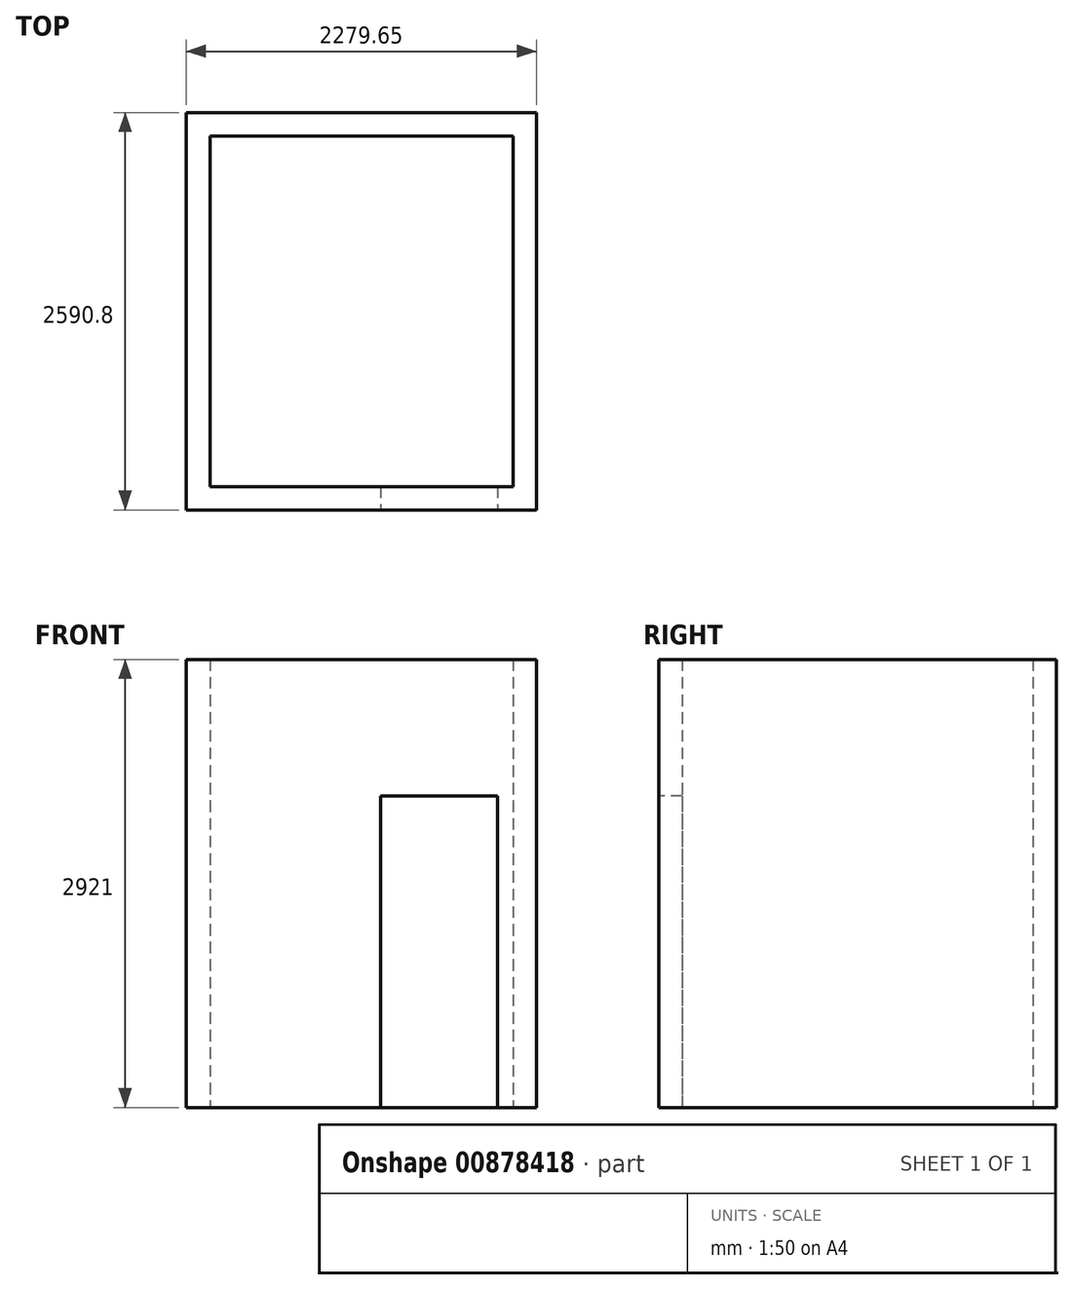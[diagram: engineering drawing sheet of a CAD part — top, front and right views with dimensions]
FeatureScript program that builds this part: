
annotation { "Feature Type Name" : "Feature", "Feature Type Description" : "" }
export const myFeature = defineFeature(function(context is Context, id is Id, definition is map)
    precondition{}
    {
        {
            var Q0;
            Q0=qCreatedBy(makeId("Top.planeOp"),FACE);
            var sketch = newSketch(context, id + "F0", { "sketchPlane" : qUnion([Q0])});
            skLineSegment(sketch, "E0", {"start": v(0, 0) * mm, "end": v(-101.6, 0) * mm});
            skLineSegment(sketch, "E1", {"start": v(-101.6, 0) * mm, "end": v(-101.6, -152.4) * mm});
            skLineSegment(sketch, "E2", {"start": v(0, 0) * mm, "end": v(0, 2286) * mm});
            skLineSegment(sketch, "E3", {"start": v(0, 2286) * mm, "end": v(-1974.85, 2286) * mm});
            skLineSegment(sketch, "E4", {"start": v(-1974.85, 2286) * mm, "end": v(-1974.85, 0) * mm});
            skLineSegment(sketch, "E5", {"start": v(-1974.85, 0) * mm, "end": v(-863.6, 0) * mm});
            skLineSegment(sketch, "E6", {"start": v(-863.6, 0) * mm, "end": v(-863.6, -152.4) * mm});
            skLineSegment(sketch, "E7", {"start": v(-863.6, -152.4) * mm, "end": v(-2127.25, -152.4) * mm});
            skLineSegment(sketch, "E8", {"start": v(-2127.25, -152.4) * mm, "end": v(-2127.25, 2438.4) * mm});
            skLineSegment(sketch, "E9", {"start": v(-2127.25, 2438.4) * mm, "end": v(152.4, 2438.4) * mm});
            skLineSegment(sketch, "E10", {"start": v(152.4, 2438.4) * mm, "end": v(152.4, -152.4) * mm});
            skLineSegment(sketch, "E11", {"start": v(152.4, -152.4) * mm, "end": v(-101.6, -152.4) * mm});
            skSolve(sketch);
        }
        {
            var Q0;
            Q0=makeQuery(id+"F0.imprint","IMPRINT",FACE,{"disambiguationData":[TD([[makeQuery(id+"F0.imprint","IMPRINT",EDGE,{"derivedFrom":sQuery(id+"F0.wireOp",EDGE,"E0")}),1.0]])]});
            extrude(context, id + "F1", {"entities" : qUnion([Q0]), "depth" : 2032 * mm, "offsetDistance" : 25.4 * mm});
        }
        {
            var Q0;
            Q0=makeQuery(id+"F1.opExtrude","CAP_FACE",FACE,{"disambiguationData":[OSD([sQuery(id+"F0.wireOp",EDGE,"E0"),sQuery(id+"F0.wireOp",EDGE,"E1"),sQuery(id+"F0.wireOp",EDGE,"E2"),sQuery(id+"F0.wireOp",EDGE,"E3"),sQuery(id+"F0.wireOp",EDGE,"E4"),sQuery(id+"F0.wireOp",EDGE,"E5"),sQuery(id+"F0.wireOp",EDGE,"E6"),sQuery(id+"F0.wireOp",EDGE,"E7"),sQuery(id+"F0.wireOp",EDGE,"E8"),sQuery(id+"F0.wireOp",EDGE,"E9"),sQuery(id+"F0.wireOp",EDGE,"E10"),sQuery(id+"F0.wireOp",EDGE,"E11")])],"isStart":false});
            var sketch = newSketch(context, id + "F2", { "sketchPlane" : qUnion([Q0])});
            skLineSegment(sketch, "E12", {"start": v(-2127.25, -152.4) * mm, "end": v(152.4, -152.4) * mm});
            skLineSegment(sketch, "E13", {"start": v(152.4, -152.4) * mm, "end": v(152.4, 2438.4) * mm});
            skLineSegment(sketch, "E14", {"start": v(152.4, 2438.4) * mm, "end": v(-2127.25, 2438.4) * mm});
            skLineSegment(sketch, "E15", {"start": v(-2127.25, 2438.4) * mm, "end": v(-2127.25, -152.4) * mm});
            skLineSegment(sketch, "E16", {"start": v(0, 0) * mm, "end": v(0, 2286) * mm});
            skLineSegment(sketch, "E17", {"start": v(0, 2286) * mm, "end": v(-1974.85, 2286) * mm});
            skLineSegment(sketch, "E18", {"start": v(-1974.85, 2286) * mm, "end": v(-1974.85, 0) * mm});
            skLineSegment(sketch, "E19", {"start": v(-1974.85, 0) * mm, "end": v(0, 0) * mm});
            skSolve(sketch);
        }
        {
            var Q0;
            Q0 = qSketchRegion(id + "F2", true);
            extrude(context, id + "F3", {"entities" : qUnion([Q0]), "operationType" : NewBodyOperationType.ADD, "depth" : 889 * mm, "offsetDistance" : 25.4 * mm});
        }
    });
